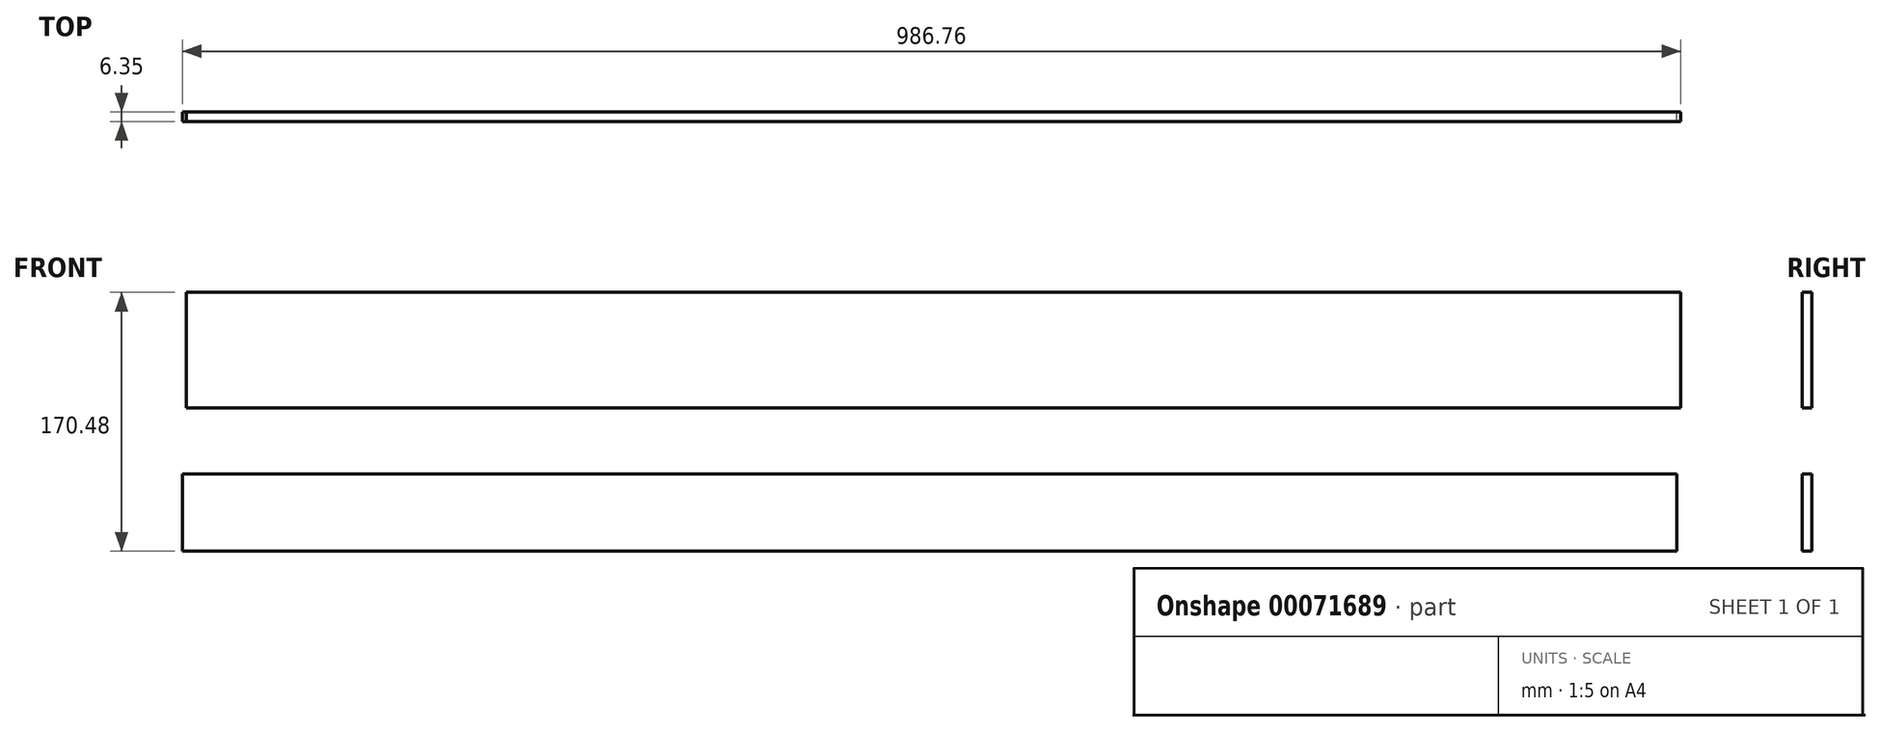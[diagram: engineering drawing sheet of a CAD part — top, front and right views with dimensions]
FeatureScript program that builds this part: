
annotation { "Feature Type Name" : "Feature", "Feature Type Description" : "" }
export const myFeature = defineFeature(function(context is Context, id is Id, definition is map)
    precondition{}
    {
        {
            var Q0;
            Q0=qCreatedBy(makeId("Front.planeOp"),FACE);
            var sketch = newSketch(context, id + "F0", { "sketchPlane" : qUnion([Q0])});
            skLineSegment(sketch, "E0.bottom", {"start": v(672.7, 119.53) * mm, "end": v(-311.48, 119.53) * mm});
            skLineSegment(sketch, "E0.top", {"start": v(672.7, 43.33) * mm, "end": v(-311.48, 43.33) * mm});
            skLineSegment(sketch, "E0.left", {"start": v(672.7, 119.53) * mm, "end": v(672.7, 43.33) * mm});
            skLineSegment(sketch, "E0.right", {"start": v(-311.48, 119.53) * mm, "end": v(-311.48, 43.33) * mm});
            skLineSegment(sketch, "E1.bottom", {"start": v(670.11, -0.15) * mm, "end": v(-314.06, -0.15) * mm});
            skLineSegment(sketch, "E1.top", {"start": v(670.11, -50.95) * mm, "end": v(-314.06, -50.95) * mm});
            skLineSegment(sketch, "E1.left", {"start": v(670.11, -0.15) * mm, "end": v(670.11, -50.95) * mm});
            skLineSegment(sketch, "E1.right", {"start": v(-314.06, -0.15) * mm, "end": v(-314.06, -50.95) * mm});
            skSolve(sketch);
        }
        {
            var Q0;
            Q0=makeQuery(id+"F0.imprint","IMPRINT",FACE,{"disambiguationData":[TD([[makeQuery(id+"F0.imprint","IMPRINT",EDGE,{"derivedFrom":sQuery(id+"F0.wireOp",EDGE,"E0.bottom")}),1.0]])]});
            var Q1;
            Q1=makeQuery(id+"F0.imprint","IMPRINT",FACE,{"disambiguationData":[TD([[makeQuery(id+"F0.imprint","IMPRINT",EDGE,{"derivedFrom":sQuery(id+"F0.wireOp",EDGE,"E1.bottom")}),1.0]])]});
            extrude(context, id + "F1", {"entities" : qUnion([Q0, Q1]), "depth" : 6.35 * mm});
        }
    });
